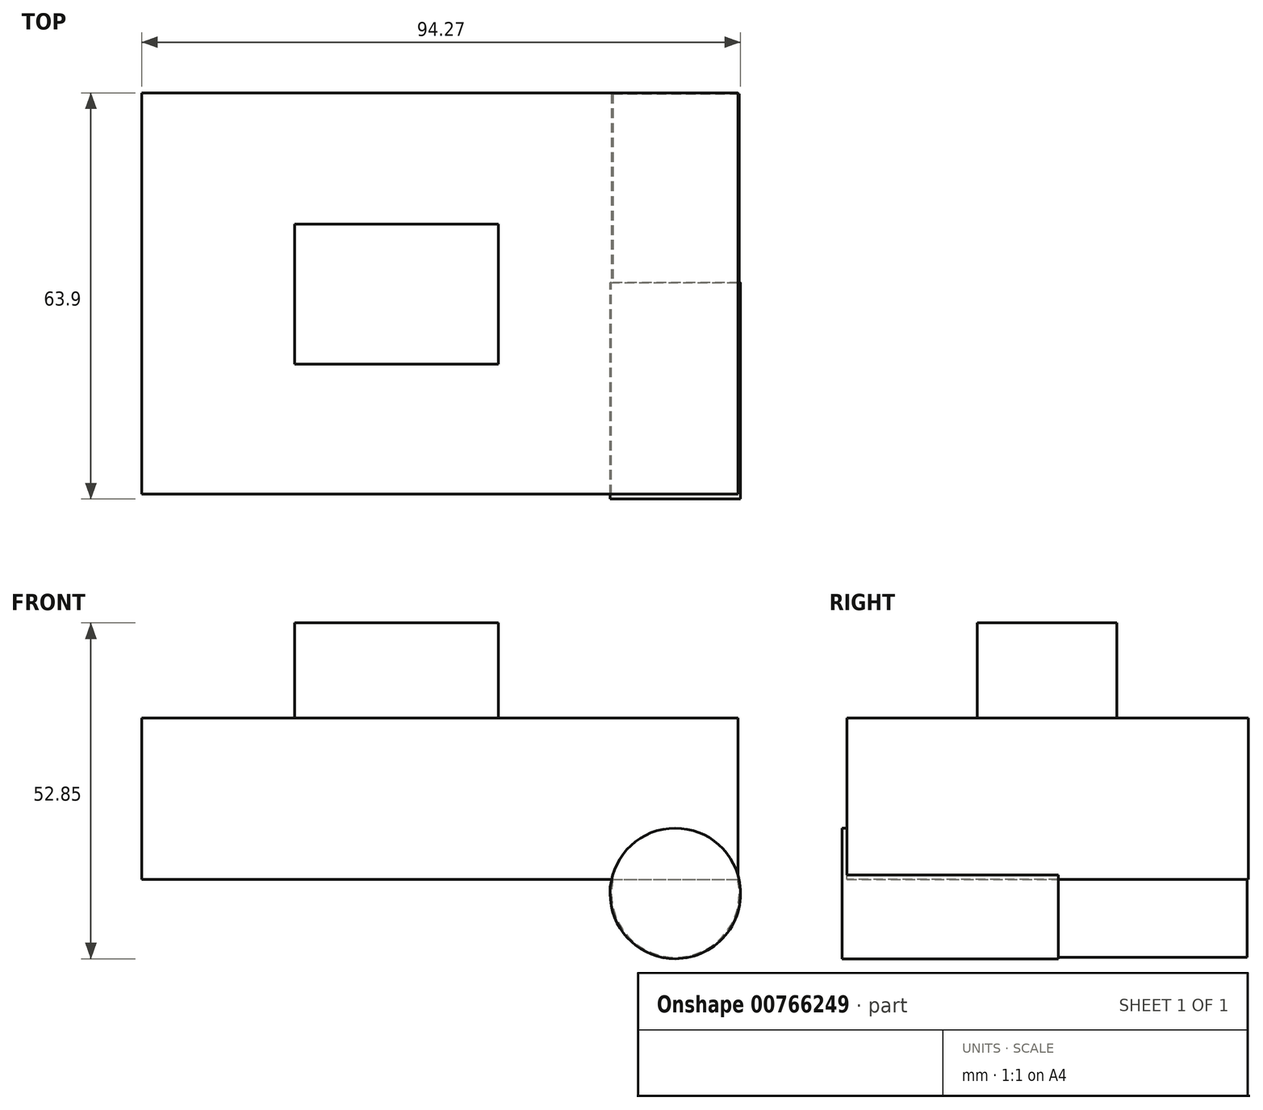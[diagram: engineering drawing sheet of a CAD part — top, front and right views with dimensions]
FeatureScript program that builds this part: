
annotation { "Feature Type Name" : "Feature", "Feature Type Description" : "" }
export const myFeature = defineFeature(function(context is Context, id is Id, definition is map)
    precondition{}
    {
        {
            var Q0;
            Q0=qCreatedBy(makeId("Top.planeOp"),FACE);
            var sketch = newSketch(context, id + "F0", { "sketchPlane" : qUnion([Q0])});
            skLineSegment(sketch, "E0.bottom", {"start": v(-37.64, 29.86) * mm, "end": v(56.22, 29.86) * mm});
            skLineSegment(sketch, "E0.top", {"start": v(-37.64, -33.27) * mm, "end": v(56.22, -33.27) * mm});
            skLineSegment(sketch, "E0.left", {"start": v(-37.64, 29.86) * mm, "end": v(-37.64, -33.27) * mm});
            skLineSegment(sketch, "E0.right", {"start": v(56.22, 29.86) * mm, "end": v(56.22, -33.27) * mm});
            skSolve(sketch);
        }
        {
            var Q0;
            Q0=makeQuery(id+"F0.imprint","IMPRINT",FACE,{"disambiguationData":[TD([[makeQuery(id+"F0.imprint","IMPRINT",EDGE,{"derivedFrom":sQuery(id+"F0.wireOp",EDGE,"E0.bottom")}),-1.0]])]});
            extrude(context, id + "F1", {"entities" : qUnion([Q0]), "depth" : 25.4 * mm, "offsetDistance" : 25.4 * mm});
        }
        {
            var Q0;
            Q0=qCreatedBy(makeId("Front.planeOp"),FACE);
            var sketch = newSketch(context, id + "F2", { "sketchPlane" : qUnion([Q0])});
            skCircle(sketch, "E1", {"center": v(46.36, -2.18) * mm, "radius": 10.28 * mm});
            skSolve(sketch);
        }
        {
            var Q0;
            Q0=makeQuery(id+"F2.imprint","IMPRINT",FACE,{"disambiguationData":[TD([[makeQuery(id+"F2.imprint","IMPRINT",EDGE,{"derivedFrom":sQuery(id+"F2.wireOp",EDGE,"E1")}),1.0]])]});
            extrude(context, id + "F3", {"entities" : qUnion([Q0]), "operationType" : NewBodyOperationType.ADD, "depth" : 34.04 * mm, "offsetDistance" : 25.4 * mm});
        }
        {
            var Q0;
            Q0=makeQuery(id+"F3.opExtrude","CAP_FACE",FACE,{"disambiguationData":[OSD([sQuery(id+"F2.wireOp",EDGE,"E1")])],"isStart":true});
            var sketch = newSketch(context, id + "F4", { "sketchPlane" : qUnion([Q0])});
            skCircle(sketch, "E2", {"center": v(-46.36, -2.18) * mm, "radius": 10.06 * mm});
            skSolve(sketch);
        }
        {
            var Q0;
            {var subQ0=sQuery(id+"F4.wireOp",EDGE,"E2");var subQ1=makeQuery(id+"F3.boolean.opBoolean","INTERSECT",EDGE,{"derivedFrom":[makeQuery(id+"F1.opExtrude","CAP_FACE",FACE,{"disambiguationData":[OSD([sQuery(id+"F0.wireOp",EDGE,"E0.bottom"),sQuery(id+"F0.wireOp",EDGE,"E0.top"),sQuery(id+"F0.wireOp",EDGE,"E0.left"),sQuery(id+"F0.wireOp",EDGE,"E0.right")])],"isStart":true}),makeQuery(id+"F3.opExtrude","CAP_FACE",FACE,{"disambiguationData":[OSD([sQuery(id+"F2.wireOp",EDGE,"E1")])],"isStart":true})]});var subQ2=makeQuery(id+"F4.imprint","INTERSECT",VERTEX,{"disambiguationData":[OD(0.0)],"derivedFrom":[subQ1,subQ0]});Q0=makeQuery(id+"F4.imprint","IMPRINT",FACE,{"disambiguationData":[TD([[makeQuery(id+"F4.imprint","IMPRINT",EDGE,{"disambiguationData":[TD([[subQ2,-1.0]])],"derivedFrom":subQ0}),1.0]])]});}
            extrude(context, id + "F5", {"entities" : qUnion([Q0]), "operationType" : NewBodyOperationType.ADD, "depth" : 29.72 * mm, "offsetDistance" : 25.4 * mm});
        }
        {
            var Q0;
            Q0=makeQuery(id+"F1.opExtrude","CAP_FACE",FACE,{"disambiguationData":[OSD([sQuery(id+"F0.wireOp",EDGE,"E0.bottom"),sQuery(id+"F0.wireOp",EDGE,"E0.top"),sQuery(id+"F0.wireOp",EDGE,"E0.left"),sQuery(id+"F0.wireOp",EDGE,"E0.right")])],"isStart":false});
            var sketch = newSketch(context, id + "F6", { "sketchPlane" : qUnion([Q0])});
            skLineSegment(sketch, "E3.bottom", {"start": v(18.49, 9.2) * mm, "end": v(-13.56, 9.2) * mm});
            skLineSegment(sketch, "E3.top", {"start": v(18.49, -12.8) * mm, "end": v(-13.56, -12.8) * mm});
            skLineSegment(sketch, "E3.left", {"start": v(18.49, 9.2) * mm, "end": v(18.49, -12.8) * mm});
            skLineSegment(sketch, "E3.right", {"start": v(-13.56, 9.2) * mm, "end": v(-13.56, -12.8) * mm});
            skSolve(sketch);
        }
        {
            var Q0;
            Q0=makeQuery(id+"F6.imprint","IMPRINT",FACE,{"disambiguationData":[TD([[makeQuery(id+"F6.imprint","IMPRINT",EDGE,{"derivedFrom":sQuery(id+"F6.wireOp",EDGE,"E3.bottom")}),1.0]])]});
            extrude(context, id + "F7", {"entities" : qUnion([Q0]), "operationType" : NewBodyOperationType.ADD, "depth" : 15 * mm, "offsetDistance" : 25.4 * mm});
        }
    });
